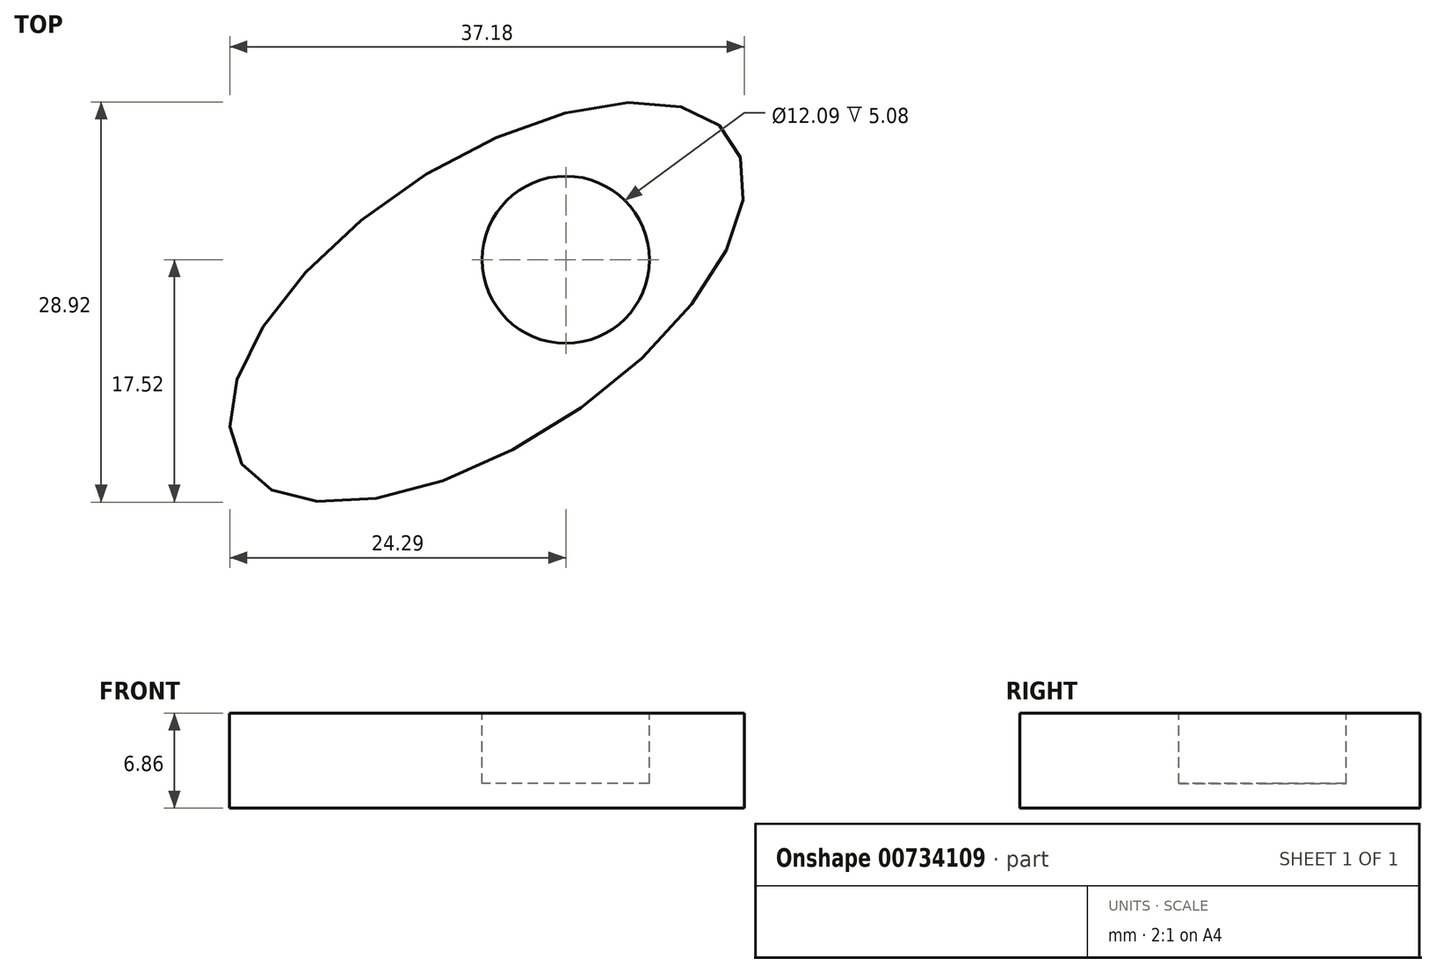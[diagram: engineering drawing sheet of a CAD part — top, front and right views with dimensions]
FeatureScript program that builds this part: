
annotation { "Feature Type Name" : "Feature", "Feature Type Description" : "" }
export const myFeature = defineFeature(function(context is Context, id is Id, definition is map)
    precondition{}
    {
        {
            var Q0;
            Q0=qCreatedBy(makeId("Top.planeOp"),FACE);
            var sketch = newSketch(context, id + "F0", { "sketchPlane" : qUnion([Q0])});
            skEllipse(sketch, "E0", {"center": v(0, 0) * mm, "majorRadius": 21.25 * mm, "minorRadius": 10.15 * mm, "majorAxis": v(-0.83, -0.55)});
            skSolve(sketch);
        }
        {
            var Q0;
            Q0 = qSketchRegion(id + "F0", true);
            extrude(context, id + "F1", {"entities" : qUnion([Q0]), "depth" : 6.86 * mm, "offsetDistance" : 25.4 * mm});
        }
        {
            var Q0;
            Q0=makeQuery(id+"F1.opExtrude","CAP_FACE",FACE,{"disambiguationData":[OSD([sQuery(id+"F0.wireOp",EDGE,"E0")])],"isStart":false});
            var sketch = newSketch(context, id + "F2", { "sketchPlane" : qUnion([Q0])});
            skCircle(sketch, "E1", {"center": v(5.7, 3.06) * mm, "radius": 6.05 * mm});
            skSolve(sketch);
        }
        {
            var Q0;
            Q0 = qSketchRegion(id + "F2", true);
            extrude(context, id + "F3", {"entities" : qUnion([Q0]), "operationType" : NewBodyOperationType.REMOVE, "oppositeDirection" : true, "depth" : 5.08 * mm, "offsetDistance" : 25.4 * mm});
        }
    });
